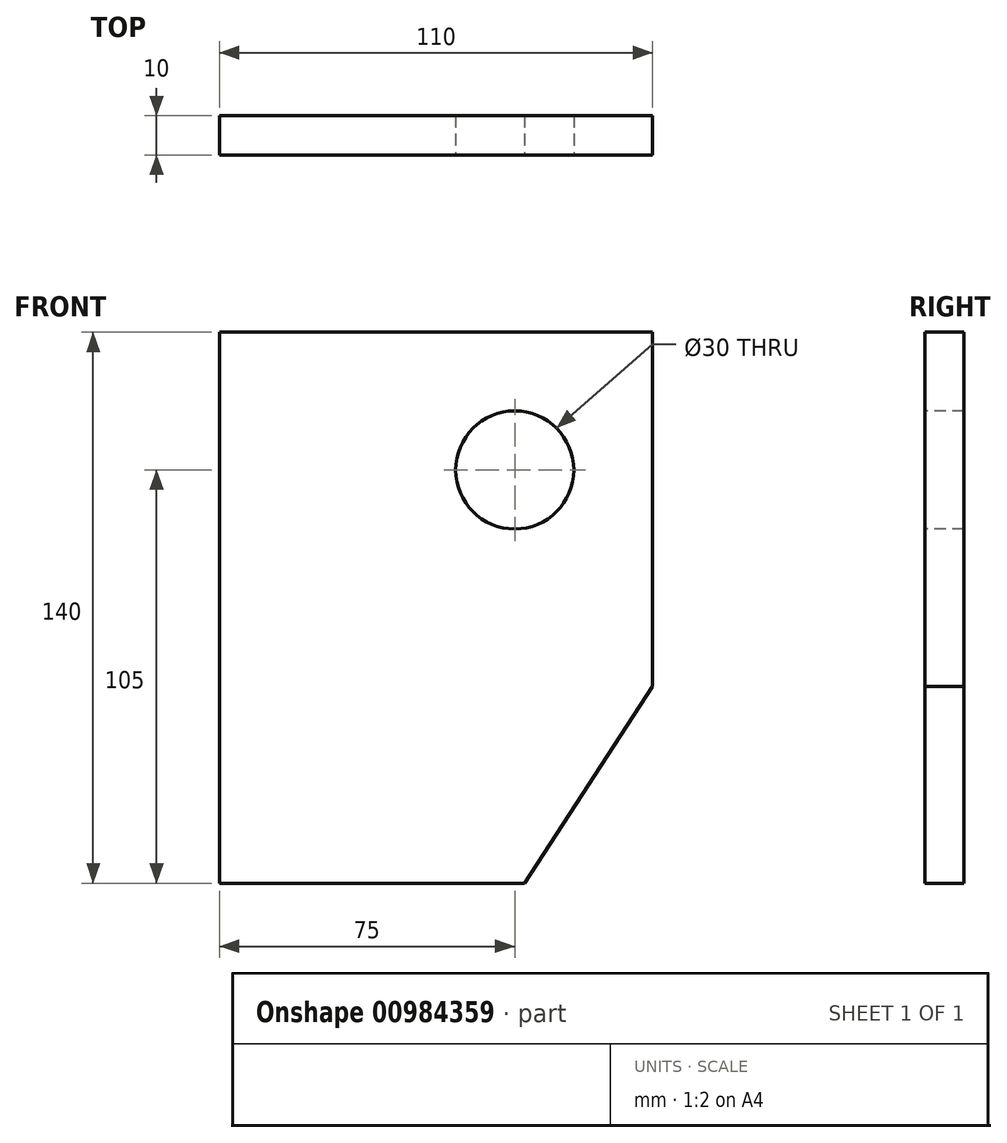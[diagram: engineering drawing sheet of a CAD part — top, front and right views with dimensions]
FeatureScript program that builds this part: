
annotation { "Feature Type Name" : "Feature", "Feature Type Description" : "" }
export const myFeature = defineFeature(function(context is Context, id is Id, definition is map)
    precondition{}
    {
        {
            var Q0;
            Q0=qCreatedBy(makeId("Front.planeOp"),FACE);
            var sketch = newSketch(context, id + "F0", { "sketchPlane" : qUnion([Q0])});
            skLineSegment(sketch, "E0.bottom", {"start": v(55, -70) * mm, "end": v(-55, -70) * mm});
            skLineSegment(sketch, "E0.top", {"start": v(55, 70) * mm, "end": v(-55, 70) * mm});
            skLineSegment(sketch, "E0.left", {"start": v(55, -70) * mm, "end": v(55, 70) * mm});
            skLineSegment(sketch, "E0.right", {"start": v(-55, -70) * mm, "end": v(-55, 70) * mm});
            skPoint(sketch, "E0.middle", {"position": v(0, 0) * mm});
            skSolve(sketch);
        }
        {
            var Q0;
            Q0=qSketchRegion(id+"F0",true);
            extrude(context, id + "F1", {"entities" : qUnion([Q0]), "depth" : 10 * mm, "offsetDistance" : 25 * mm});
        }
        {
            var Q0;
            Q0=qCreatedBy(makeId("Front.planeOp"),FACE);
            var sketch = newSketch(context, id + "F2", { "sketchPlane" : qUnion([Q0])});
            skCircle(sketch, "E1", {"center": v(20, 35) * mm, "radius": 15 * mm});
            skSolve(sketch);
        }
        {
            var Q0;
            Q0=qSketchRegion(id+"F2",true);
            extrude(context, id + "F3", {"entities" : qUnion([Q0]), "operationType" : NewBodyOperationType.REMOVE, "oppositeDirection" : true, "depth" : 25 * mm, "offsetDistance" : 25 * mm, "hasSecondDirection" : true, "secondDirectionOppositeDirection" : false, "secondDirectionDepth" : 25 * mm});
        }
        {
            var Q0;
            Q0=makeQuery(id+"F1.opExtrude","SWEPT_EDGE",EDGE,{"disambiguationData":[OSD([sQuery(id+"F0.wireOp",EDGE,"E0.bottom"),sQuery(id+"F0.wireOp",EDGE,"E0.left")])]});
            chamfer(context, id + "F4", {"entities" : qUnion([Q0]), "chamferType" : ChamferType.OFFSET_ANGLE, "width" : 50 * mm, "oppositeDirection" : false, "angle" : 33 * degree, "tangentPropagation" : true});
        }
    });
